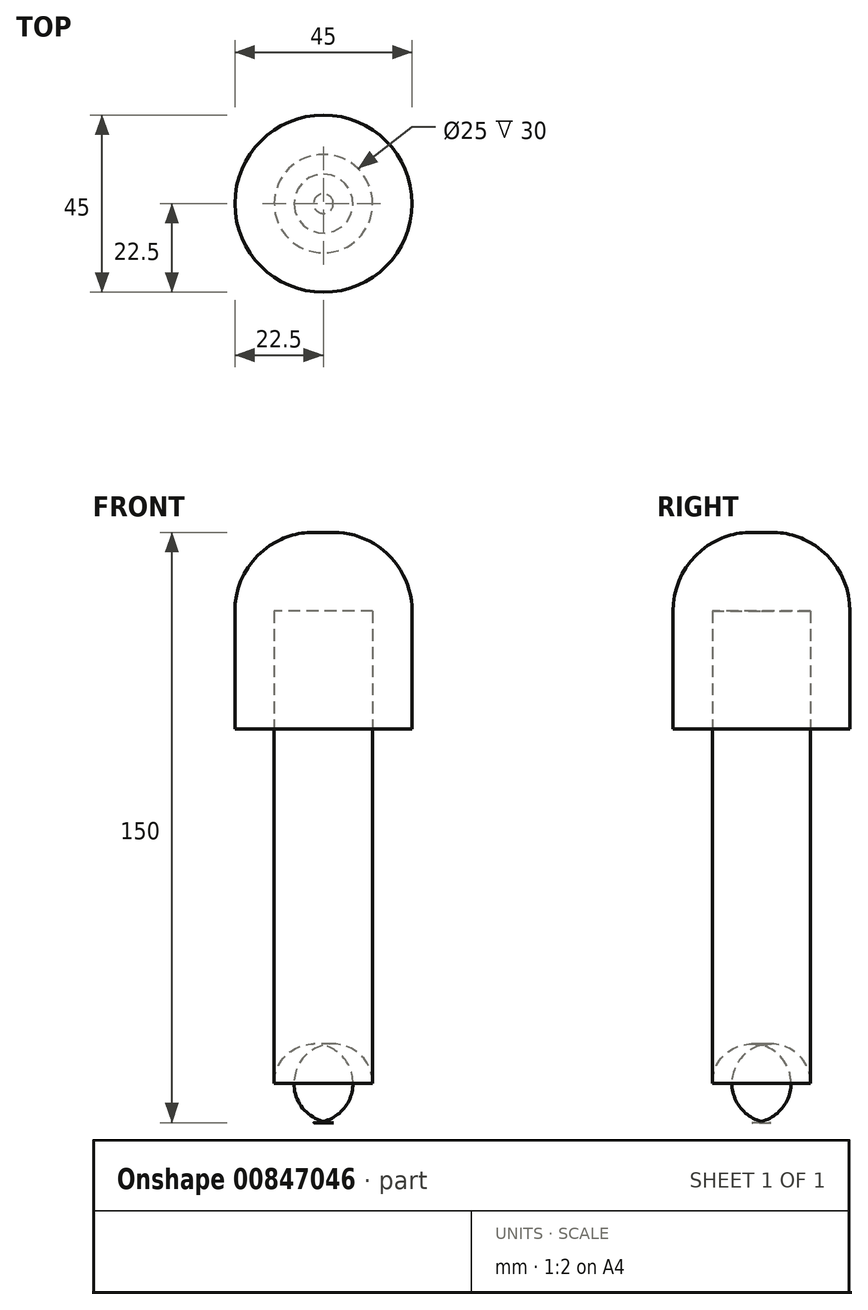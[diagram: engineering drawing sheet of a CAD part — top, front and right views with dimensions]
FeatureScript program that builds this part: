
annotation { "Feature Type Name" : "Feature", "Feature Type Description" : "" }
export const myFeature = defineFeature(function(context is Context, id is Id, definition is map)
    precondition{}
    {
        {
            var Q0;
            Q0=qCreatedBy(makeId("Top.planeOp"),FACE);
            var sketch = newSketch(context, id + "F0", { "sketchPlane" : qUnion([Q0])});
            skCircle(sketch, "E0", {"center": v(0, 0) * mm, "radius": 22.5 * mm});
            skCircle(sketch, "E1", {"center": v(0, 0) * mm, "radius": 12.5 * mm});
            skSolve(sketch);
        }
        {
            var Q0;
            Q0=makeQuery(id+"F0.imprint","IMPRINT",FACE,{"disambiguationData":[TD([[makeQuery(id+"F0.imprint","IMPRINT",EDGE,{"derivedFrom":sQuery(id+"F0.wireOp",EDGE,"E0")}),1.0]])]});
            extrude(context, id + "F1", {"entities" : qUnion([Q0]), "depth" : 30 * mm, "offsetDistance" : 25.4 * mm});
        }
        {
            var Q0;
            Q0=makeQuery(id+"F0.imprint","IMPRINT",FACE,{"disambiguationData":[TD([[makeQuery(id+"F0.imprint","IMPRINT",EDGE,{"derivedFrom":sQuery(id+"F0.wireOp",EDGE,"E1")}),1.0]])]});
            extrude(context, id + "F2", {"entities" : qUnion([Q0]), "operationType" : NewBodyOperationType.ADD, "oppositeDirection" : true, "depth" : 100 * mm, "offsetDistance" : 25.4 * mm});
        }
        {
            var Q0;
            Q0=makeQuery(id+"F2.opExtrude","CAP_FACE",FACE,{"disambiguationData":[OSD([sQuery(id+"F0.wireOp",EDGE,"E1")])],"isStart":false});
            fillet(context, id + "F3", {"entities" : qUnion([Q0]), "radius" : 10 * mm, "tangentPropagation" : true, "allowEdgeOverflow" : false});
        }
        {
            var Q0;
            Q0=makeQuery(id+"F1.opExtrude","CAP_FACE",FACE,{"disambiguationData":[OSD([sQuery(id+"F0.wireOp",EDGE,"E0"),sQuery(id+"F0.wireOp",EDGE,"E1")])],"isStart":false});
            var sketch = newSketch(context, id + "F4", { "sketchPlane" : qUnion([Q0])});
            skCircle(sketch, "E2", {"center": v(0, 0) * mm, "radius": 22.5 * mm});
            skSolve(sketch);
        }
        {
            var Q0;
            Q0=qSketchRegion(id+"F4",true);
            extrude(context, id + "F5", {"entities" : qUnion([Q0]), "operationType" : NewBodyOperationType.ADD, "depth" : 20 * mm, "offsetDistance" : 25.4 * mm});
        }
        {
            var Q0;
            Q0=makeQuery(id+"F5.opExtrude","CAP_FACE",FACE,{"disambiguationData":[OSD([sQuery(id+"F4.wireOp",EDGE,"E2")])],"isStart":false});
            fillet(context, id + "F6", {"entities" : qUnion([Q0]), "radius" : 20 * mm, "tangentPropagation" : true, "allowEdgeOverflow" : false});
        }
    });
